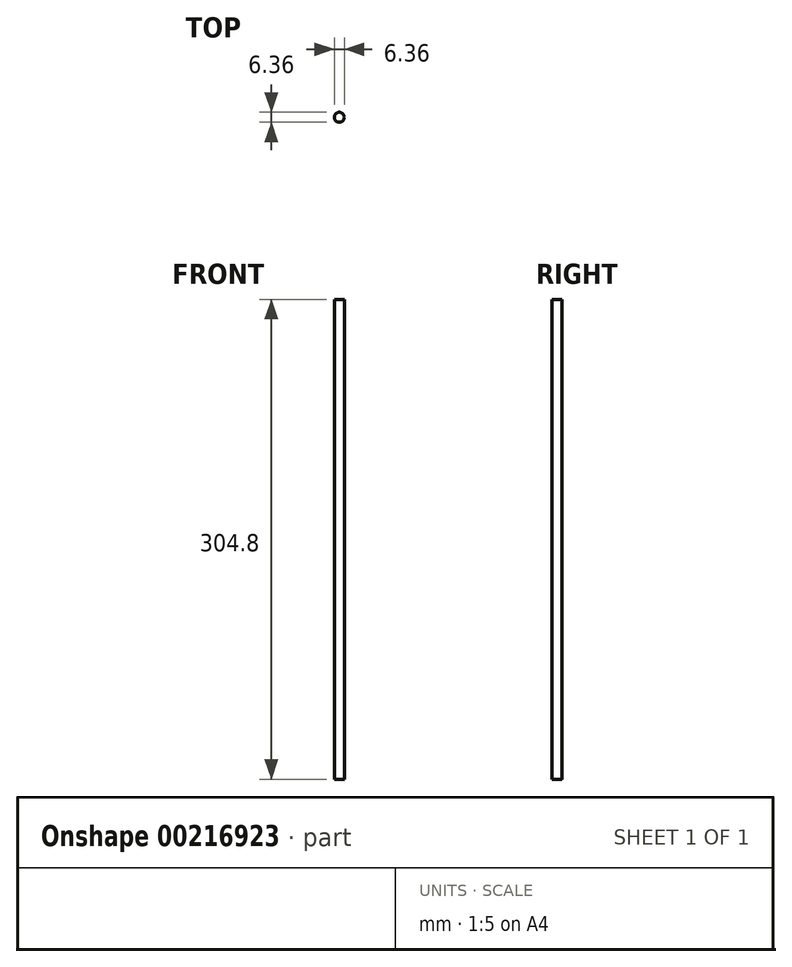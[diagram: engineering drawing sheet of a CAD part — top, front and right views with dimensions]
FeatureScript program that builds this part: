
annotation { "Feature Type Name" : "Feature", "Feature Type Description" : "" }
export const myFeature = defineFeature(function(context is Context, id is Id, definition is map)
    precondition{}
    {
        {
            var Q0;
            Q0=qCreatedBy(makeId("Top.planeOp"),FACE);
            var sketch = newSketch(context, id + "F0", { "sketchPlane" : qUnion([Q0])});
            skCircle(sketch, "E0", {"center": v(0, 0) * mm, "radius": 3.18 * mm});
            skSolve(sketch);
        }
        {
            var Q0;
            Q0 = qSketchRegion(id + "F0", true);
            extrude(context, id + "F1", {"entities" : qUnion([Q0]), "depth" : 152.4 * mm, "hasSecondDirection" : true, "secondDirectionOppositeDirection" : true, "secondDirectionDepth" : 152.4 * mm});
        }
    });
